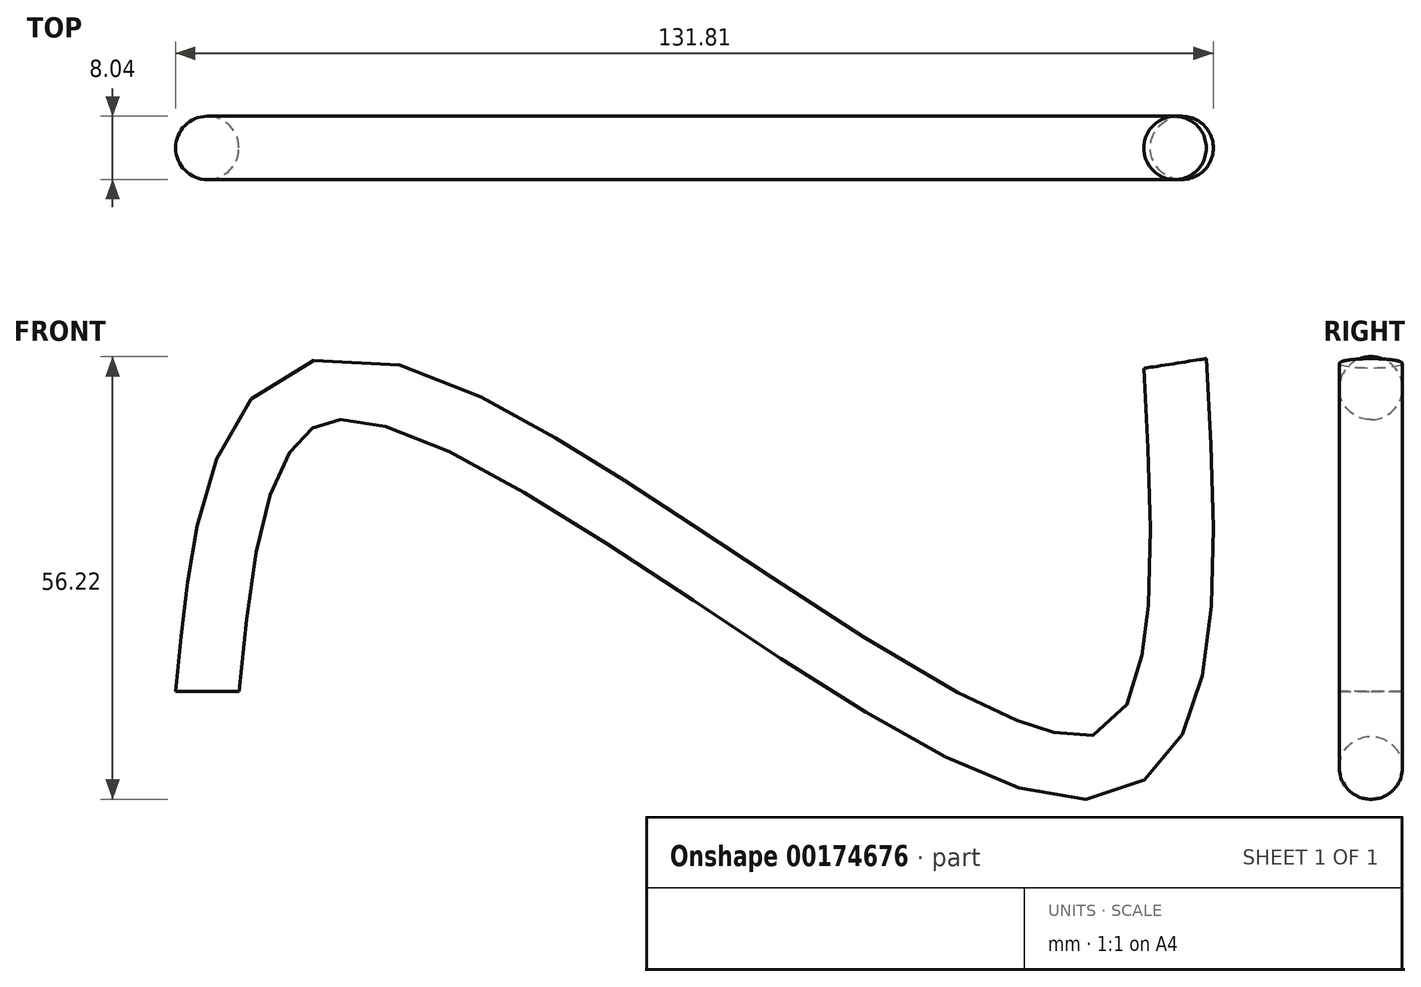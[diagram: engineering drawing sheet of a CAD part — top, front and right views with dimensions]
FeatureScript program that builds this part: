
annotation { "Feature Type Name" : "Feature", "Feature Type Description" : "" }
export const myFeature = defineFeature(function(context is Context, id is Id, definition is map)
    precondition{}
    {
        {
            var Q0;
            Q0=qCreatedBy(makeId("Front.planeOp"),FACE);
            var sketch = newSketch(context, id + "F0", { "sketchPlane" : qUnion([Q0])});
            skFitSpline(sketch, "E0", {"points": [v(-57.05, -20.1) * mm, v(-39.36, 18.4) * mm, v(54.48, -29.8) * mm, v(65.9, 21.54) * mm], "startDerivative": vector(21.07, 214.16) * mm, "endDerivative": vector(-14.24, 252.2) * mm});
            skSolve(sketch);
        }
        {
            var Q0;
            Q0=qCreatedBy(makeId("Top.planeOp"),FACE);
            var Q1;
            Q1=sQuery(id+"F0.wireOp",VERTEX,"E0.start");
            cPlane(context, id + "F1", {"entities" : qUnion([Q0, Q1]), "cplaneType" : CPlaneType.PLANE_POINT, "offset" : 25.4 * mm, "width" : 152.4 * mm, "height" : 152.4 * mm});
        }
        {
            var Q0;
            Q0=qCreatedBy(id+"F1.planeOp",FACE);
            var sketch = newSketch(context, id + "F2", { "sketchPlane" : qUnion([Q0])});
            skCircle(sketch, "E1", {"center": v(-57.05, 0) * mm, "radius": 4.02 * mm});
            skSolve(sketch);
        }
        {
            var Q0;
            Q0=makeQuery(id+"F2.imprint","IMPRINT",FACE,{"disambiguationData":[TD([[makeQuery(id+"F2.imprint","IMPRINT",EDGE,{"derivedFrom":sQuery(id+"F2.wireOp",EDGE,"E1")}),1.0]])]});
            var Q1;
            Q1=sQuery(id+"F0.wireOp",EDGE,"E0");
            sweep(context, id + "F3", {"profiles" : qUnion([Q0]), "path" : qUnion([Q1])});
        }
    });
